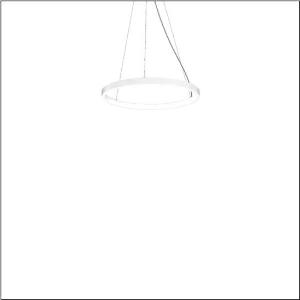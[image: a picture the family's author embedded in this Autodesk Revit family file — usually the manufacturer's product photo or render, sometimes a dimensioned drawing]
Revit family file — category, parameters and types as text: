
# Revit family: silica_r__21_ring-i_5pjbi1d1004a_4ad1
name_source: partatom
category: Lighting Fixtures
units: mm (PartAtom-declared; Revit-internal decimal feet)

## family parameters
Cut with Voids When Loaded = No
Host = Face
Light Source = No
Part Type = Normal
Room Calculation Point = No
Round Connector Dimension = Use Diameter
Shared = No

## types (1)
- Silica® 21 Ring-I (1 x LED, 3430 lm, 60 W, 3000K)
    Apparent Load = 60 VA
    CIE Flux Codes = 22 48 76 50 101
    Color Rendering = 80
    Color Temperature = 3000K
    Default Elevation = 1800 mm
    Description = Silica® 21 Ring-I, suspended luminaire, of PMMA, frosted, light emission: inner ring side luminous distribution, primary light characteristic: symmetric, installation type: suspended mounting, LED, rated luminous flux: 3.430lm, luminous efficacy: 57lm/W, light colour: 830, colour temperature: 3000K, with terminal, 5-pole, mains connection: 230V, AC/DC, 0/50..60Hz, rated input power: 60W, housing, of extruded aluminium section, traffic white (RAL 9016), diameter: 610mm, ceiling canopy, traffic white (RAL 9016), protection rating (lamp compartment): IP40, insulation class (complete): insulation class I (protective earthing), certification: CE, impact resistance: IK02, permissible operating ambient temperature: 0..+35°C, packaging unit: 1 piece
    Height = 48 mm  [stored 0.15748 ft]
    Lamp = 1 x LED
    Lamp Light Flux = 3430 lm
    Lamp Power = 60 W
    Lamp count = 1
    Length = 610 mm
    Luminous efficacy = 57 lm/W
    Manufacturer = Siteco
    ModVariant = No
    Model = 5PJBI1D1004A
    Mounting Place = Ceiling
    Mounting Type = Pendant
    Number of Poles = 1
    OnlyDefault = Yes
    Power Factor = 1
    Product Name = Silica® 21 Ring-I
    Product group = suspended luminaire
    ProductGroupID = 904
    Protection Class = Protection class I
    Protection Degree = IP 40
    RLX_Detail_Level = 1
    RLX_Emergency_Light_Flux = 0 lm
    RLX_Emergency_Type = 0
    RLX_Emergency_Type_DB = No
    RlxData = <blob elided: 10465 chars, md5=5807bf4e>
    Socket = socket
    Standby Power = 0 W
    System Light Flux = 3430 lm
    System Power = 60 W
    Type Comments = Product without accessories
    Type Image = l_1258363.jpg
    URL = http://relux.com
    VarID = ---
    Voltage = 0 V
    Weight = 0.00 kg
    Width = 0 mm  [stored 0 ft]

note: [stored X ft] marks values corroborated as IEEE doubles in the binary element streams (Revit-internal decimal feet)

## geometry (parser evidence)
native form markers: Sweep x13
no freeform markers — native parametric forms only
